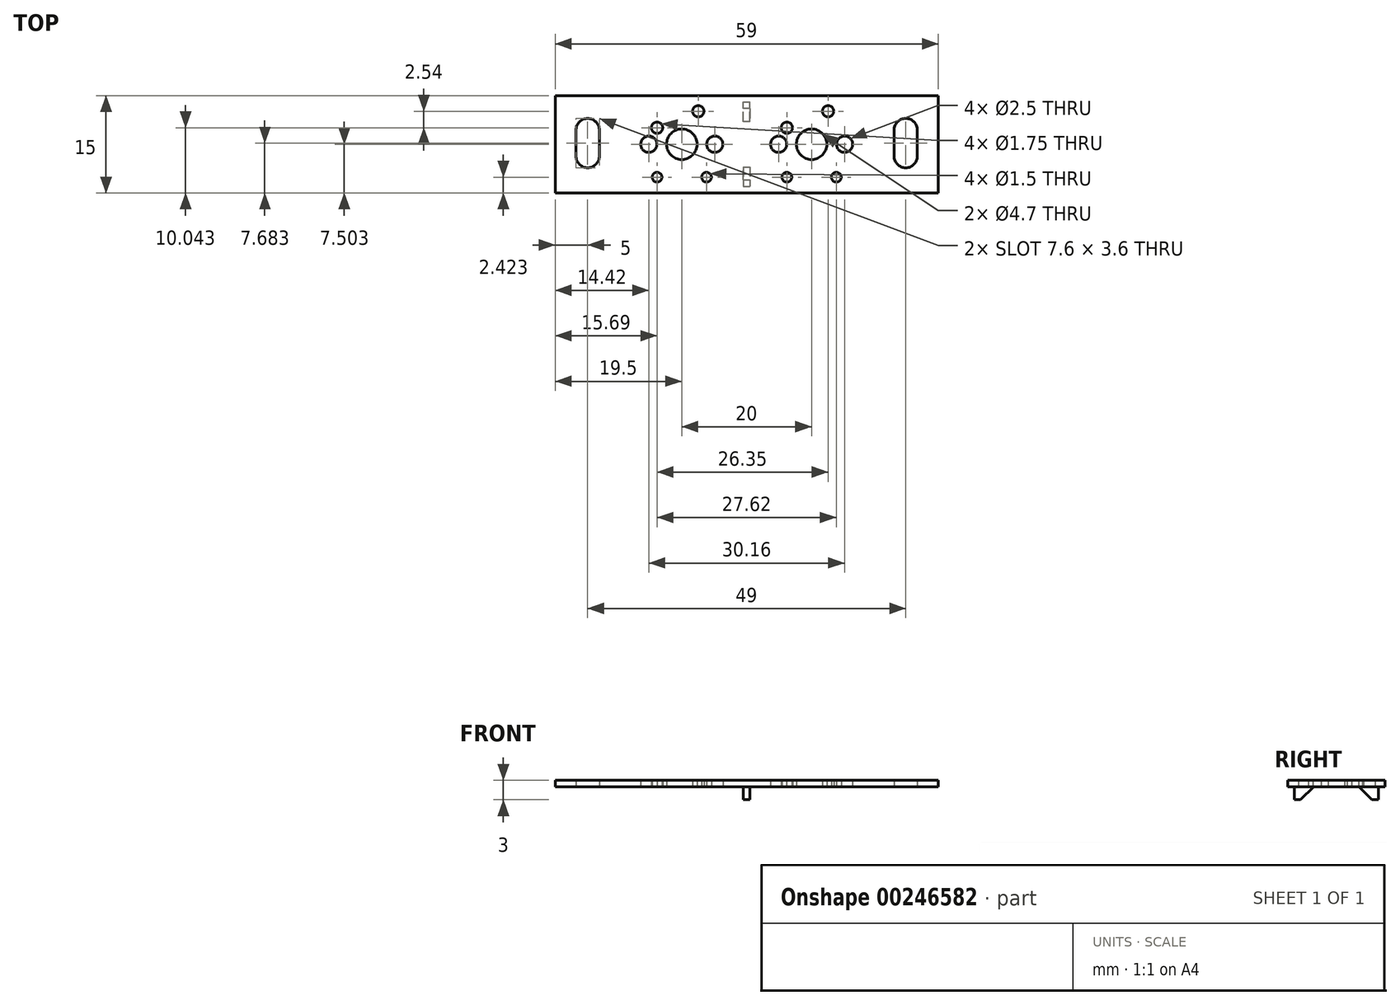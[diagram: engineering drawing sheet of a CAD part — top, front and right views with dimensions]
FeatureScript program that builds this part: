
annotation { "Feature Type Name" : "Feature", "Feature Type Description" : "" }
export const myFeature = defineFeature(function(context is Context, id is Id, definition is map)
    precondition{}
    {
        {
            var Q0;
            Q0=qCreatedBy(makeId("Top.planeOp"),FACE);
            var sketch = newSketch(context, id + "F0", { "sketchPlane" : qUnion([Q0])});
            skCircle(sketch, "E0", {"center": v(0, 12.32) * mm, "radius": 2.35 * mm});
            skCircle(sketch, "E1", {"center": v(-5.08, 12.32) * mm, "radius": 1.25 * mm});
            skCircle(sketch, "E2.MirrorC", {"center": v(5.08, 12.32) * mm, "radius": 1.25 * mm});
            skCircle(sketch, "E3", {"center": v(-3.81, 14.86) * mm, "radius": 0.88 * mm});
            skCircle(sketch, "E4", {"center": v(2.54, 17.4) * mm, "radius": 0.88 * mm});
            skCircle(sketch, "E5", {"center": v(-3.81, 7.24) * mm, "radius": 0.75 * mm});
            skCircle(sketch, "E6.MirrorC", {"center": v(3.81, 7.24) * mm, "radius": 0.75 * mm});
            skLineSegment(sketch, "E7", {"start": v(10, 27.9) * mm, "end": v(10, -3.67) * mm, "construction": true});
            skCircle(sketch, "E8.MirrorC", {"center": v(20, 12.32) * mm, "radius": 2.35 * mm});
            skCircle(sketch, "E9.MirrorC", {"center": v(14.92, 12.32) * mm, "radius": 1.25 * mm});
            skCircle(sketch, "E10.MirrorC", {"center": v(25.08, 12.32) * mm, "radius": 1.25 * mm});
            skCircle(sketch, "E11.MirrorC", {"center": v(16.2, 7.24) * mm, "radius": 0.75 * mm});
            skCircle(sketch, "E12.MirrorC", {"center": v(23.81, 7.24) * mm, "radius": 0.75 * mm});
            skCircle(sketch, "E13", {"center": v(16.2, 14.86) * mm, "radius": 0.88 * mm});
            skCircle(sketch, "E14", {"center": v(22.54, 17.4) * mm, "radius": 0.88 * mm});
            skLineSegment(sketch, "E15.bottom", {"start": v(-19.5, 19.82) * mm, "end": v(39.5, 19.82) * mm});
            skLineSegment(sketch, "E15.top", {"start": v(-19.5, 4.82) * mm, "end": v(39.5, 4.82) * mm});
            skLineSegment(sketch, "E15.left", {"start": v(-19.5, 19.82) * mm, "end": v(-19.5, 4.82) * mm});
            skLineSegment(sketch, "E15.right", {"start": v(39.5, 19.82) * mm, "end": v(39.5, 4.82) * mm});
            skPoint(sketch, "E15.middle", {"position": v(10, 12.32) * mm});
            skPoint(sketch, "E15.middle.positionSnap0", {"position": v(10, 12.11) * mm});
            skPoint(sketch, "E15.centerSnap0", {"position": v(10, 12.11) * mm});
            skArc(sketch, "E16", {"start": v(-12.7, 14.5) * mm, "mid": v(-14.5, 16.3) * mm, "end": v(-16.3, 14.5) * mm});
            skArc(sketch, "E17", {"start": v(-16.3, 10.5) * mm, "mid": v(-14.5, 8.7) * mm, "end": v(-12.7, 10.5) * mm});
            skLineSegment(sketch, "E18", {"start": v(-16.3, 14.5) * mm, "end": v(-16.3, 10.5) * mm});
            skLineSegment(sketch, "E19", {"start": v(-12.7, 10.5) * mm, "end": v(-12.7, 14.5) * mm});
            skLineSegment(sketch, "E20.MirrorCS", {"start": v(32.7, 10.5) * mm, "end": v(32.7, 14.5) * mm});
            skLineSegment(sketch, "E21.MirrorCS", {"start": v(36.3, 14.5) * mm, "end": v(36.3, 10.5) * mm});
            skArc(sketch, "E22.MirrorCS", {"start": v(36.3, 10.5) * mm, "mid": v(34.5, 8.7) * mm, "end": v(32.7, 10.5) * mm});
            skArc(sketch, "E23.MirrorCS", {"start": v(32.7, 14.5) * mm, "mid": v(34.5, 16.3) * mm, "end": v(36.3, 14.5) * mm});
            skSolve(sketch);
        }
        {
            var Q0;
            Q0=makeQuery(id+"F0.imprint","IMPRINT",FACE,{"disambiguationData":[TD([[makeQuery(id+"F0.imprint","IMPRINT",EDGE,{"derivedFrom":sQuery(id+"F0.wireOp",EDGE,"E0")}),-1.0]])]});
            extrude(context, id + "F1", {"entities" : qUnion([Q0]), "depth" : 1 * mm});
        }
        {
            var Q0;
            Q0=makeQuery(id+"F1.opExtrude","CAP_FACE",FACE,{"disambiguationData":[OSD([sQuery(id+"F0.wireOp",EDGE,"E0"),sQuery(id+"F0.wireOp",EDGE,"E1"),sQuery(id+"F0.wireOp",EDGE,"E2.MirrorC"),sQuery(id+"F0.wireOp",EDGE,"E3"),sQuery(id+"F0.wireOp",EDGE,"E4"),sQuery(id+"F0.wireOp",EDGE,"E5"),sQuery(id+"F0.wireOp",EDGE,"E6.MirrorC"),sQuery(id+"F0.wireOp",EDGE,"E8.MirrorC"),sQuery(id+"F0.wireOp",EDGE,"E9.MirrorC"),sQuery(id+"F0.wireOp",EDGE,"E10.MirrorC"),sQuery(id+"F0.wireOp",EDGE,"E11.MirrorC"),sQuery(id+"F0.wireOp",EDGE,"E12.MirrorC"),sQuery(id+"F0.wireOp",EDGE,"E13"),sQuery(id+"F0.wireOp",EDGE,"E14"),sQuery(id+"F0.wireOp",EDGE,"E15.bottom"),sQuery(id+"F0.wireOp",EDGE,"E15.top"),sQuery(id+"F0.wireOp",EDGE,"E15.left"),sQuery(id+"F0.wireOp",EDGE,"E15.right"),sQuery(id+"F0.wireOp",EDGE,"E16"),sQuery(id+"F0.wireOp",EDGE,"E17"),sQuery(id+"F0.wireOp",EDGE,"E18"),sQuery(id+"F0.wireOp",EDGE,"E19"),sQuery(id+"F0.wireOp",EDGE,"E20.MirrorCS"),sQuery(id+"F0.wireOp",EDGE,"E21.MirrorCS"),sQuery(id+"F0.wireOp",EDGE,"E22.MirrorCS"),sQuery(id+"F0.wireOp",EDGE,"E23.MirrorCS")])],"isStart":false});
            var sketch = newSketch(context, id + "F2", { "sketchPlane" : qUnion([Q0])});
            skLineSegment(sketch, "E24.0.0", {"start": v(-19.5, 19.82) * mm, "end": v(-19.5, 4.82) * mm});
            skLineSegment(sketch, "E24.0.1", {"start": v(-19.5, 4.82) * mm, "end": v(39.5, 4.82) * mm});
            skLineSegment(sketch, "E24.0.2", {"start": v(39.5, 4.82) * mm, "end": v(39.5, 19.82) * mm});
            skLineSegment(sketch, "E24.0.3", {"start": v(39.5, 19.82) * mm, "end": v(-19.5, 19.82) * mm});
            skLineSegment(sketch, "E25.bottom", {"start": v(-19.5, 19.82) * mm, "end": v(39.5, 19.82) * mm});
            skLineSegment(sketch, "E25.top", {"start": v(-19.5, 18.82) * mm, "end": v(39.5, 18.82) * mm});
            skLineSegment(sketch, "E25.left", {"start": v(-19.5, 19.82) * mm, "end": v(-19.5, 18.82) * mm});
            skLineSegment(sketch, "E25.right", {"start": v(39.5, 19.82) * mm, "end": v(39.5, 18.82) * mm});
            skLineSegment(sketch, "E26.top", {"start": v(-19.5, 5.82) * mm, "end": v(39.5, 5.82) * mm});
            skLineSegment(sketch, "E26.left", {"start": v(-19.5, 4.82) * mm, "end": v(-19.5, 5.82) * mm});
            skLineSegment(sketch, "E26.right", {"start": v(39.5, 4.82) * mm, "end": v(39.5, 5.82) * mm});
            skLineSegment(sketch, "E27", {"start": v(10, 5.82) * mm, "end": v(10, 9.82) * mm});
            skLineSegment(sketch, "E28", {"start": v(10, 9.82) * mm, "end": v(9.5, 9.82) * mm});
            skLineSegment(sketch, "E29", {"start": v(9.5, 9.82) * mm, "end": v(9.5, 5.82) * mm});
            skLineSegment(sketch, "E30", {"start": v(10, 9.82) * mm, "end": v(10.5, 9.82) * mm});
            skLineSegment(sketch, "E31", {"start": v(10.5, 9.82) * mm, "end": v(10.5, 5.82) * mm});
            skLineSegment(sketch, "E32", {"start": v(5.08, 12.32) * mm, "end": v(14.92, 12.32) * mm, "construction": true});
            skLineSegment(sketch, "E33.MirrorCS", {"start": v(9.5, 14.82) * mm, "end": v(9.5, 18.82) * mm});
            skLineSegment(sketch, "E34.MirrorCS", {"start": v(10.5, 14.82) * mm, "end": v(10.5, 18.82) * mm});
            skLineSegment(sketch, "E35.MirrorCS", {"start": v(10, 14.82) * mm, "end": v(9.5, 14.82) * mm});
            skLineSegment(sketch, "E36", {"start": v(10, 14.82) * mm, "end": v(10.5, 14.82) * mm});
            skSolve(sketch);
        }
        {
            var Q0;
            Q0=makeQuery(id+"F2.imprint","IMPRINT",FACE,{"disambiguationData":[TD([[makeQuery(id+"F2.imprint","IMPRINT",EDGE,{"derivedFrom":sQuery(id+"F2.wireOp",EDGE,"E25.bottom")}),-1.0]])]});
            var Q1;
            Q1=makeQuery(id+"F2.imprint","IMPRINT",FACE,{"disambiguationData":[TD([[makeQuery(id+"F2.imprint","IMPRINT",EDGE,{"derivedFrom":sQuery(id+"F2.wireOp",EDGE,"E24.0.1")}),1.0]])]});
            var Q2;
            {var subQ0=sQuery(id+"F2.wireOp",EDGE,"E27");Q2=makeQuery(id+"F2.imprint","IMPRINT",FACE,{"disambiguationData":[TD([[makeQuery(id+"F2.imprint","IMPRINT",EDGE,{"derivedFrom":subQ0}),-1.0]])]});}
            var Q3;
            {var subQ1=sQuery(id+"F2.wireOp",EDGE,"E33.MirrorCS");Q3=makeQuery(id+"F2.imprint","IMPRINT",FACE,{"disambiguationData":[TD([[makeQuery(id+"F2.imprint","IMPRINT",EDGE,{"derivedFrom":subQ1}),-1.0]])]});}
            var Q4;
            {var subQ0=sQuery(id+"F2.wireOp",EDGE,"E27");Q4=makeQuery(id+"F2.imprint","IMPRINT",FACE,{"disambiguationData":[TD([[makeQuery(id+"F2.imprint","IMPRINT",EDGE,{"derivedFrom":subQ0}),1.0]])]});}
            extrude(context, id + "F3", {"entities" : qUnion([Q0, Q1, Q2, Q3, Q4]), "operationType" : NewBodyOperationType.ADD, "oppositeDirection" : true, "depth" : 3 * mm});
        }
        {
            var Q0;
            Q0=makeQuery(id+"F3.opExtrude","CAP_EDGE",EDGE,{"disambiguationData":[OSD([sQuery(id+"F2.wireOp",EDGE,"E28"),sQuery(id+"F2.wireOp",EDGE,"E30")])],"isStart":false});
            var Q1;
            Q1=makeQuery(id+"F3.opExtrude","CAP_EDGE",EDGE,{"disambiguationData":[OSD([sQuery(id+"F2.wireOp",EDGE,"E35.MirrorCS"),sQuery(id+"F2.wireOp",EDGE,"E36")])],"isStart":false});
            chamfer(context, id + "F4", {"entities" : qUnion([Q0, Q1]), "width" : 3 * mm, "tangentPropagation" : true});
        }
    });
